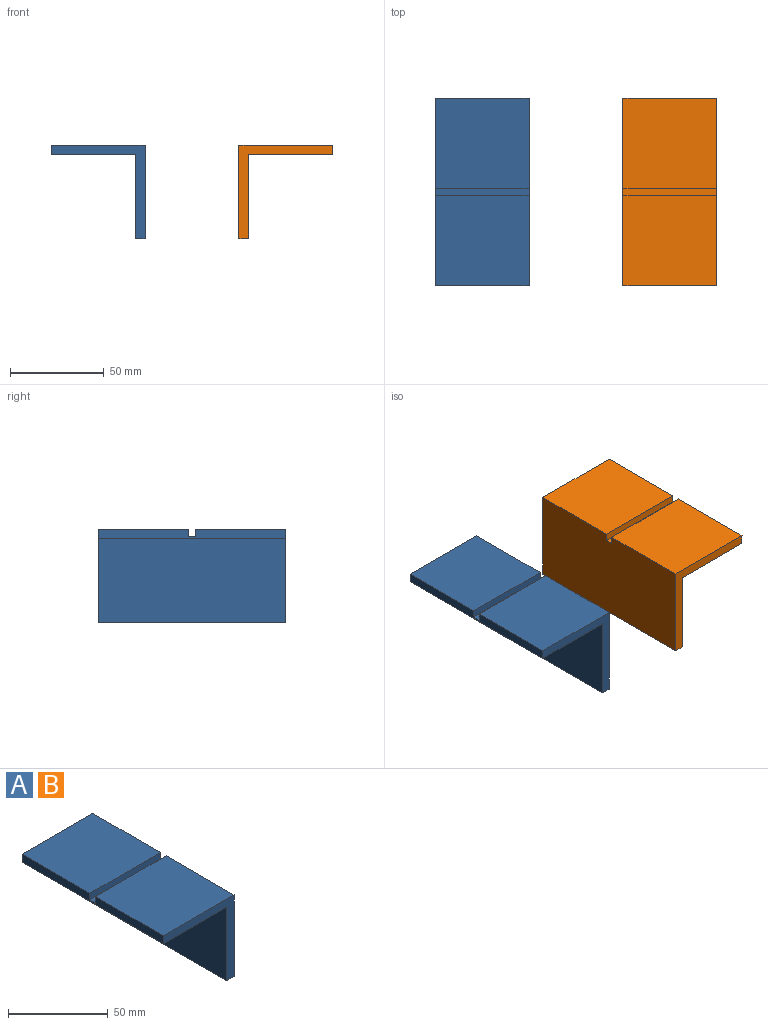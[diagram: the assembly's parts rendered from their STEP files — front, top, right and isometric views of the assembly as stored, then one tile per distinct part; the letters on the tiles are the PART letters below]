
ASSEMBLY  parts=2 mates=1
PART A: 12 faces, bbox 50x100x50 mm
  f0: plane 50x48mm, normal (0,0,1), area 2400mm2, adj f1,f5,f7,f10
  f1: plane 100x5mm, normal (-1,0,0), area 484mm2, adj f0,f2,f6,f7,f8,f9,f10,f11
  f2: plane 100x45mm, normal (0,0,-1), area 4500mm2, adj f1,f3,f7,f8
  f3: plane 100x45mm, normal (-1,0,0), area 4500mm2, adj f2,f4,f7,f8
  f4: plane 100x5mm, normal (0,0,-1), area 500mm2, adj f3,f5,f7,f8
  f5: plane 100x50mm, normal (1,0,0), area 4984mm2, adj f0,f4,f6,f7,f8,f9,f10,f11
  f6: plane 50x48mm, normal (0,0,1), area 2400mm2, adj f1,f5,f8,f9
  f7: plane 50x50mm, normal (0,-1,0), area 475mm2, adj f0,f1,f2,f3,f4,f5
  f8: plane 50x50mm, normal (0,1,0), area 475mm2, adj f1,f2,f3,f4,f5,f6
  f9: plane 50x4mm, normal (0,-1,0), area 200mm2, adj f1,f5,f6,f11
  f10: plane 50x4mm, normal (0,1,0), area 200mm2, adj f0,f1,f5,f11
  f11: plane 50x4mm, normal (0,0,1), area 200mm2, adj f1,f5,f9,f10
PART B: same geometry as A
PLACE A t=(76.23,-119.18,-22.8)mm
PLACE B rot(axis=(0,0,1),180deg) t=(126.23,-119.18,-22.8)mm
MATE parallel B.f5 <-> A.f5  axis (-1,0,0) through (126.23,-119.18,2.12)mm
